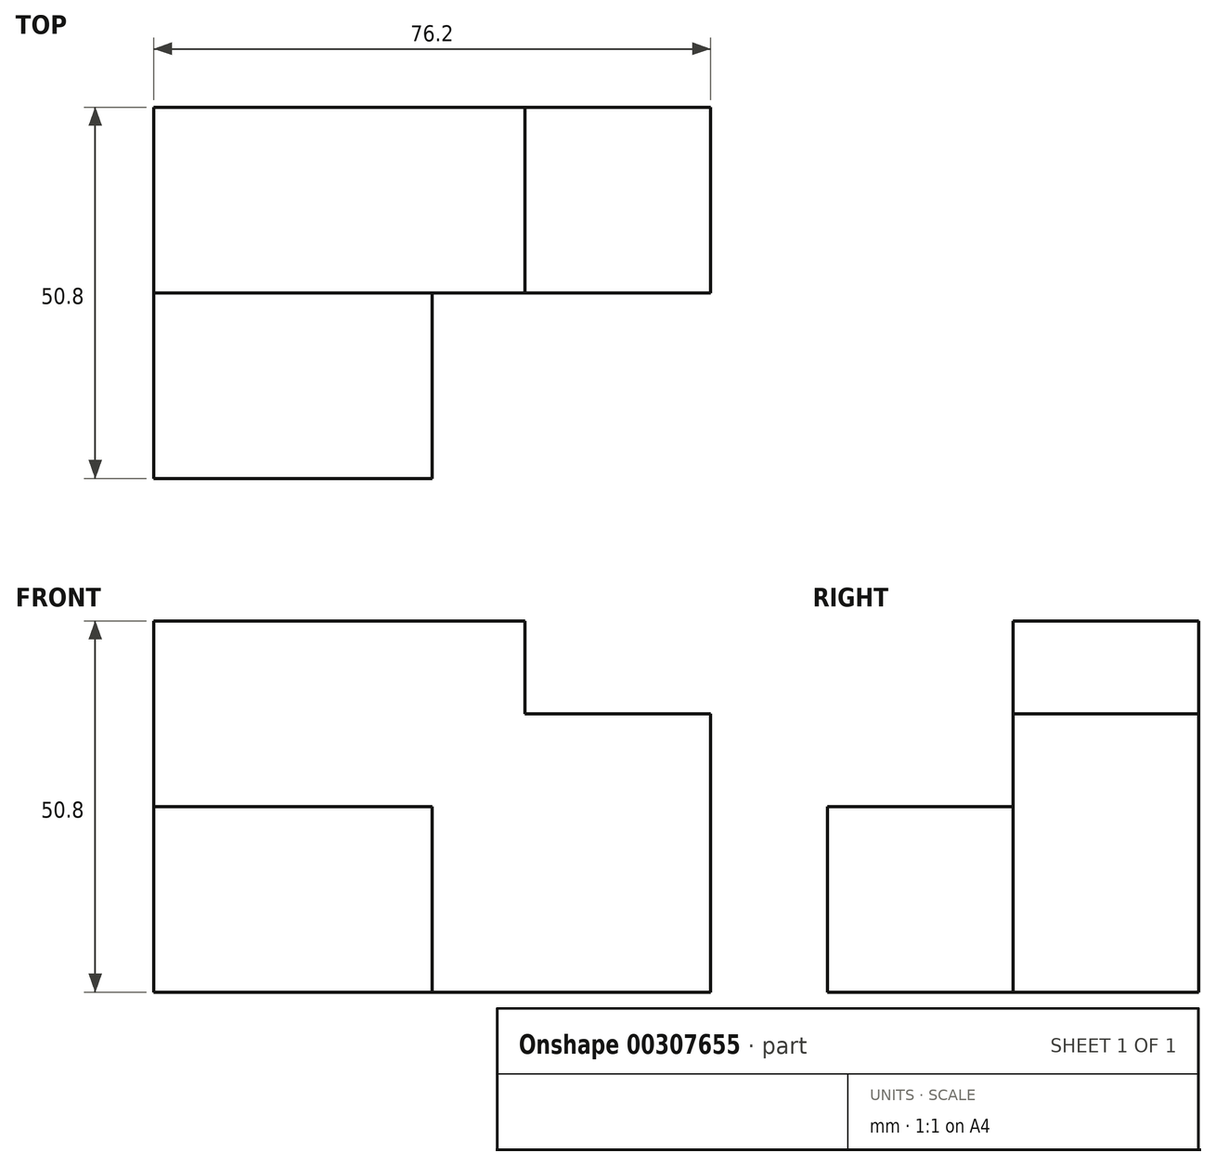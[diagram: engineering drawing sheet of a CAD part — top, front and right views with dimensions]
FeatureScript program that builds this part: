
annotation { "Feature Type Name" : "Feature", "Feature Type Description" : "" }
export const myFeature = defineFeature(function(context is Context, id is Id, definition is map)
    precondition{}
    {
        {
            var Q0;
            Q0=qCreatedBy(makeId("Front.planeOp"),FACE);
            var sketch = newSketch(context, id + "F0", { "sketchPlane" : qUnion([Q0])});
            skLineSegment(sketch, "E0", {"start": v(-28.27, 43.86) * mm, "end": v(22.53, 43.86) * mm});
            skLineSegment(sketch, "E1", {"start": v(22.53, 43.86) * mm, "end": v(22.53, 31.16) * mm});
            skLineSegment(sketch, "E2", {"start": v(22.53, 31.16) * mm, "end": v(47.93, 31.16) * mm});
            skLineSegment(sketch, "E3", {"start": v(-28.27, 43.86) * mm, "end": v(-28.27, -6.94) * mm});
            skLineSegment(sketch, "E4", {"start": v(-28.27, -6.94) * mm, "end": v(47.93, -6.94) * mm});
            skLineSegment(sketch, "E5", {"start": v(47.93, -6.94) * mm, "end": v(47.93, 31.16) * mm});
            skSolve(sketch);
        }
        {
            var Q0;
            Q0 = qSketchRegion(id + "F0", true);
            extrude(context, id + "F1", {"entities" : qUnion([Q0]), "depth" : 25.4 * mm});
        }
        {
            var Q0;
            Q0=makeQuery(id+"F1.opExtrude","CAP_FACE",FACE,{"disambiguationData":[OSD([sQuery(id+"F0.wireOp",EDGE,"E0"),sQuery(id+"F0.wireOp",EDGE,"E1"),sQuery(id+"F0.wireOp",EDGE,"E2"),sQuery(id+"F0.wireOp",EDGE,"E3"),sQuery(id+"F0.wireOp",EDGE,"E4"),sQuery(id+"F0.wireOp",EDGE,"E5")])],"isStart":false});
            var sketch = newSketch(context, id + "F2", { "sketchPlane" : qUnion([Q0])});
            skLineSegment(sketch, "E6", {"start": v(-28.27, -6.94) * mm, "end": v(-28.27, 18.46) * mm});
            skLineSegment(sketch, "E7", {"start": v(-28.27, 18.46) * mm, "end": v(9.83, 18.46) * mm});
            skLineSegment(sketch, "E8", {"start": v(9.83, 18.46) * mm, "end": v(9.83, -6.94) * mm});
            skLineSegment(sketch, "E9", {"start": v(9.83, -6.94) * mm, "end": v(-28.27, -6.94) * mm});
            skSolve(sketch);
        }
        {
            var Q0;
            Q0 = qSketchRegion(id + "F2", true);
            extrude(context, id + "F3", {"entities" : qUnion([Q0]), "operationType" : NewBodyOperationType.ADD, "depth" : 25.4 * mm});
        }
    });
